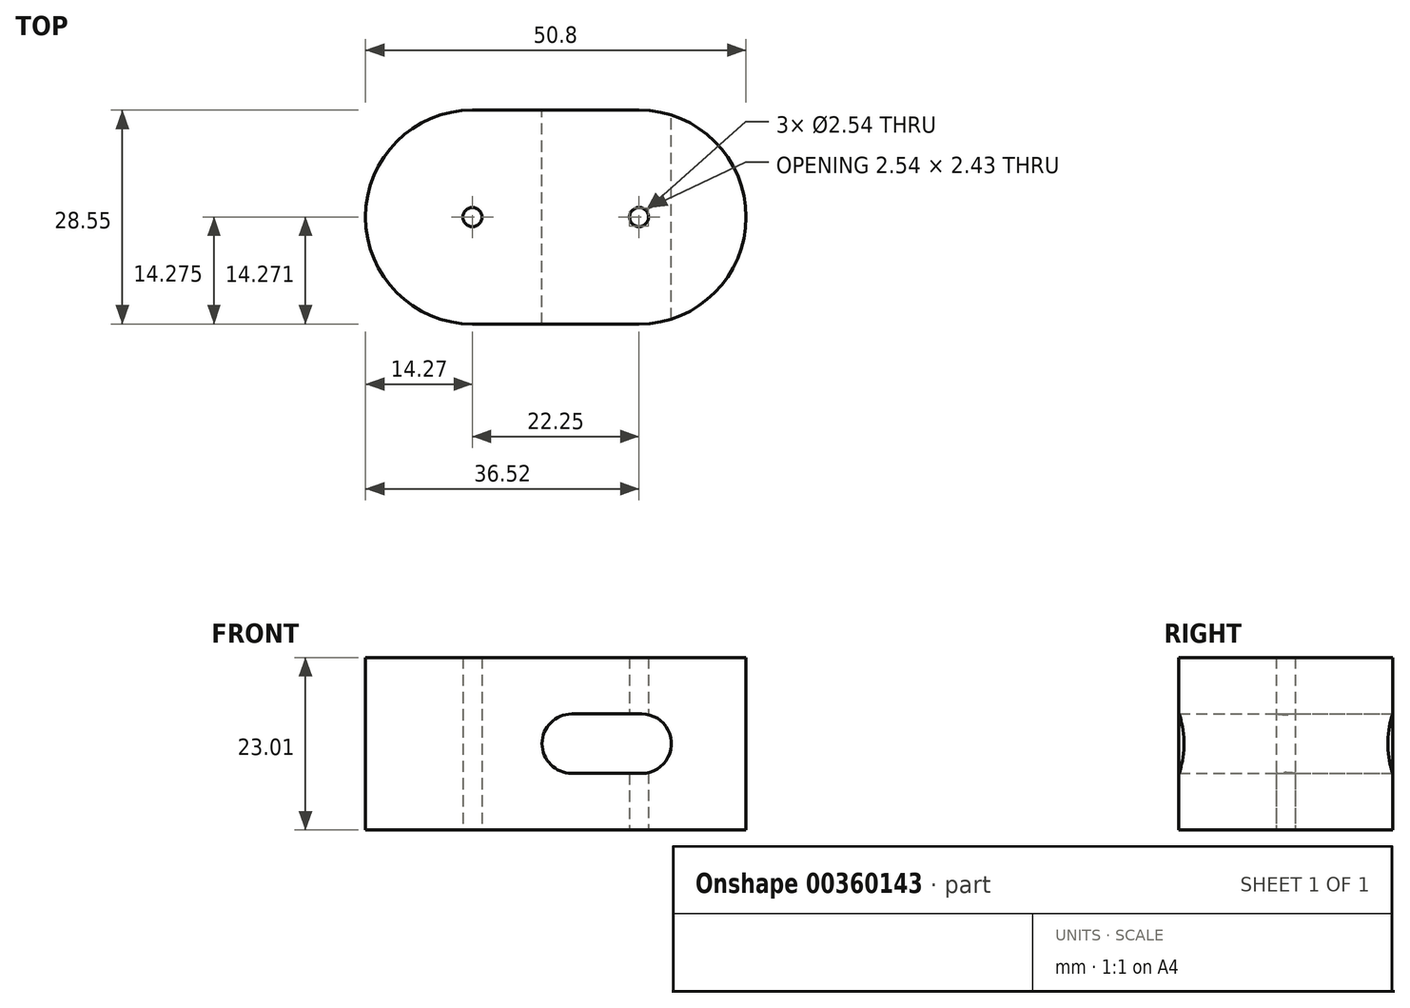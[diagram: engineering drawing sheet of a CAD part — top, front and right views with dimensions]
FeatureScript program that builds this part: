
annotation { "Feature Type Name" : "Feature", "Feature Type Description" : "" }
export const myFeature = defineFeature(function(context is Context, id is Id, definition is map)
    precondition{}
    {
        {
            var Q0;
            Q0=qCreatedBy(makeId("Top.planeOp"),FACE);
            var sketch = newSketch(context, id + "F0", { "sketchPlane" : qUnion([Q0])});
            skLineSegment(sketch, "E0.bottom", {"start": v(0, 0) * mm, "end": v(22.25, 0) * mm});
            skLineSegment(sketch, "E0.top", {"start": v(0, 28.55) * mm, "end": v(22.25, 28.55) * mm});
            skLineSegment(sketch, "E0.left", {"start": v(0, 0) * mm, "end": v(0, 28.55) * mm, "construction": true});
            skLineSegment(sketch, "E0.right", {"start": v(22.25, 0) * mm, "end": v(22.25, 28.55) * mm, "construction": true});
            skArc(sketch, "E1", {"start": v(0, 28.55) * mm, "mid": v(-14.27, 14.27) * mm, "end": v(0, 0) * mm});
            skArc(sketch, "E2", {"start": v(22.25, 0) * mm, "mid": v(36.53, 14.27) * mm, "end": v(22.25, 28.55) * mm});
            skCircle(sketch, "E3", {"center": v(0, 14.27) * mm, "radius": 1.27 * mm});
            skCircle(sketch, "E4", {"center": v(22.25, 14.27) * mm, "radius": 1.27 * mm});
            skSolve(sketch);
        }
        {
            var Q0;
            Q0=makeQuery(id+"F0.imprint","IMPRINT",FACE,{"disambiguationData":[TD([[makeQuery(id+"F0.imprint","IMPRINT",EDGE,{"derivedFrom":sQuery(id+"F0.wireOp",EDGE,"E0.bottom")}),1.0]])]});
            extrude(context, id + "F1", {"entities" : qUnion([Q0]), "depth" : 23.01 * mm});
        }
        {
            var Q0;
            Q0=makeQuery(id+"F1.opExtrude","SWEPT_FACE",FACE,{"disambiguationData":[OSD([sQuery(id+"F0.wireOp",EDGE,"E0.top")])]});
            var sketch = newSketch(context, id + "F2", { "sketchPlane" : qUnion([Q0])});
            skLineSegment(sketch, "E5", {"start": v(-22.25, 11.5) * mm, "end": v(0, 11.5) * mm, "construction": true});
            skLineSegment(sketch, "E6.bottom", {"start": v(-22.6, 7.54) * mm, "end": v(-13.26, 7.54) * mm});
            skLineSegment(sketch, "E6.top", {"start": v(-22.6, 15.47) * mm, "end": v(-13.26, 15.47) * mm});
            skLineSegment(sketch, "E6.left", {"start": v(-22.6, 7.54) * mm, "end": v(-22.6, 15.47) * mm, "construction": true});
            skLineSegment(sketch, "E6.right", {"start": v(-13.26, 7.54) * mm, "end": v(-13.26, 15.47) * mm, "construction": true});
            skArc(sketch, "E7", {"start": v(-22.6, 15.47) * mm, "mid": v(-26.57, 11.5) * mm, "end": v(-22.6, 7.54) * mm});
            skArc(sketch, "E8", {"start": v(-13.26, 7.54) * mm, "mid": v(-9.3, 11.5) * mm, "end": v(-13.26, 15.47) * mm});
            skSolve(sketch);
        }
        {
            var Q0;
            Q0=makeQuery(id+"F2.imprint","IMPRINT",FACE,{"disambiguationData":[TD([[makeQuery(id+"F2.imprint","IMPRINT",EDGE,{"derivedFrom":sQuery(id+"F2.wireOp",EDGE,"E6.bottom")}),1.0]])]});
            extrude(context, id + "F3", {"entities" : qUnion([Q0]), "operationType" : NewBodyOperationType.REMOVE, "oppositeDirection" : true, "depth" : 50.8 * mm});
        }
    });
